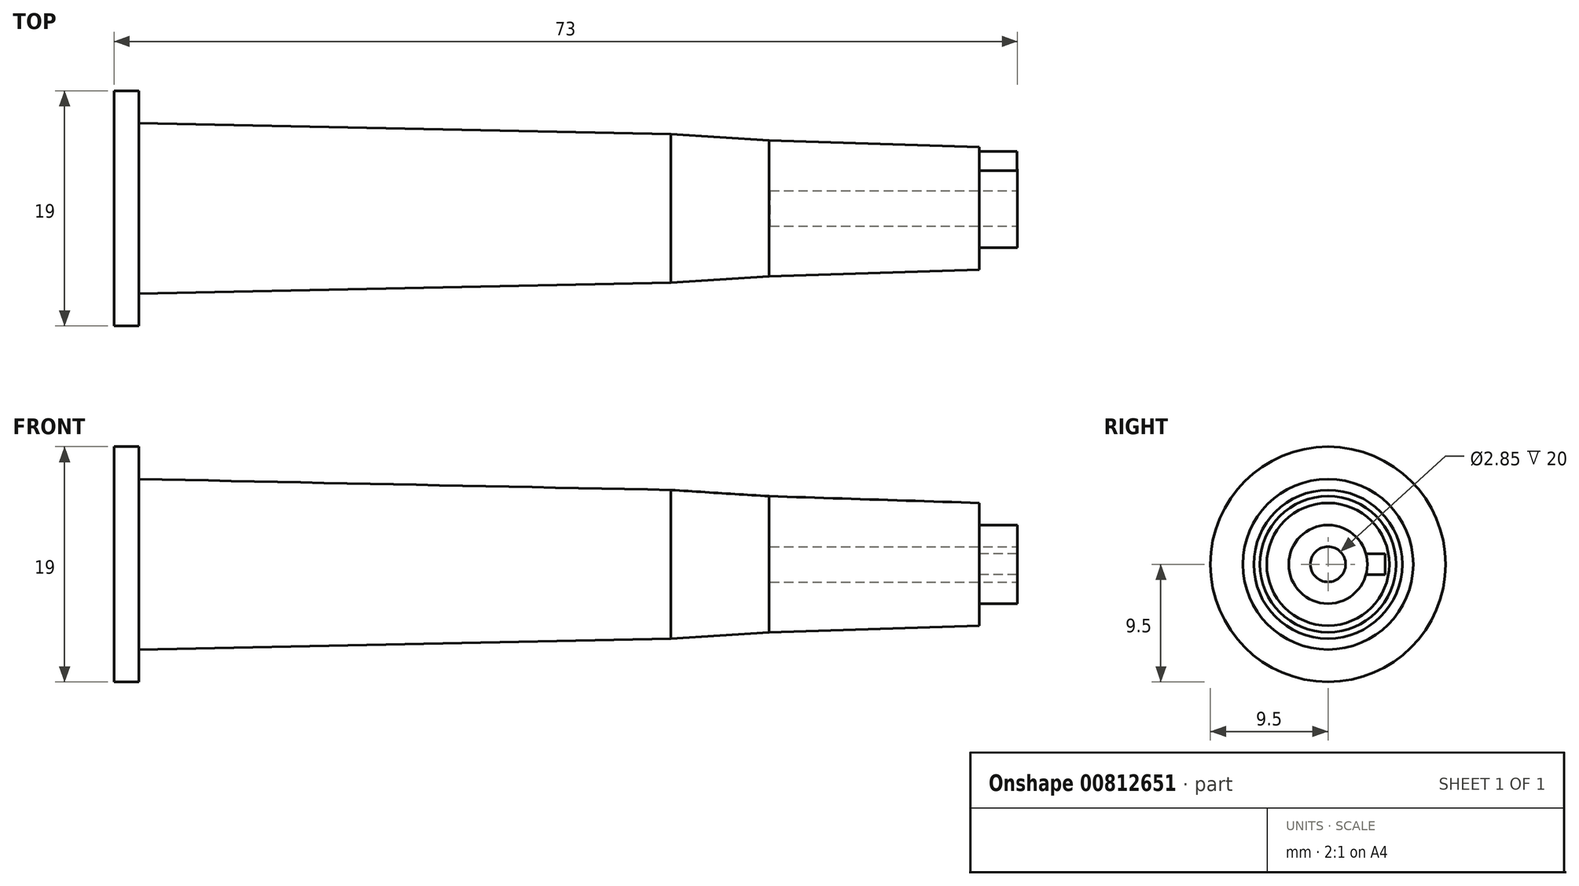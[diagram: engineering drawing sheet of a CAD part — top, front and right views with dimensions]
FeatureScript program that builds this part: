
annotation { "Feature Type Name" : "Feature", "Feature Type Description" : "" }
export const myFeature = defineFeature(function(context is Context, id is Id, definition is map)
    precondition{}
    {
        {
            var Q0;
            Q0=qCreatedBy(makeId("Front.planeOp"),FACE);
            var sketch = newSketch(context, id + "F0", { "sketchPlane" : qUnion([Q0])});
            skLineSegment(sketch, "E0", {"start": v(0, 0) * mm, "end": v(0, 9.5) * mm});
            skLineSegment(sketch, "E1", {"start": v(0, 0) * mm, "end": v(73, 0) * mm});
            skLineSegment(sketch, "E2.0", {"start": v(73, 0) * mm, "end": v(73, 3.18) * mm});
            skLineSegment(sketch, "E3.0", {"start": v(0, 9.5) * mm, "end": v(2, 9.5) * mm});
            skLineSegment(sketch, "E4", {"start": v(2, 6.88) * mm, "end": v(45, 6) * mm});
            skLineSegment(sketch, "E5.0", {"start": v(69.92, 3.18) * mm, "end": v(69.92, 4.96) * mm});
            skLineSegment(sketch, "E6", {"start": v(52.92, 5.5) * mm, "end": v(69.92, 4.96) * mm});
            skLineSegment(sketch, "E7.trimOffspring", {"start": v(69.92, 3.17) * mm, "end": v(73, 3.17) * mm});
            skLineSegment(sketch, "E8", {"start": v(45, 6) * mm, "end": v(52.92, 5.5) * mm});
            skLineSegment(sketch, "E9.trimOffspring", {"start": v(2, 6.88) * mm, "end": v(2, 9.5) * mm});
            skSolve(sketch);
        }
        {
            var Q0;
            Q0=makeQuery(id+"F0.imprint","IMPRINT",FACE,{"disambiguationData":[TD([[makeQuery(id+"F0.imprint","IMPRINT",EDGE,{"derivedFrom":sQuery(id+"F0.wireOp",EDGE,"E0")}),-1.0]])]});
            var Q1;
            Q1=sQuery(id+"F0.wireOp",EDGE,"E1");
            revolve(context, id + "F1", {"surfaceOperationType" : NewSurfaceOperationType.NEW, "entities" : qUnion([Q0]), "axis" : qUnion([Q1]), "revolveType" : RevolveType.FULL});
        }
        {
            var Q0;
            Q0=makeQuery(id+"F1.opRevolve","SWEPT_FACE",FACE,{"disambiguationData":[OSD([sQuery(id+"F0.wireOp",EDGE,"E5.0")])]});
            var sketch = newSketch(context, id + "F2", { "sketchPlane" : qUnion([Q0])});
            skLineSegment(sketch, "E10.0", {"start": v(4.61, 0.85) * mm, "end": v(4.61, -0.85) * mm});
            skLineSegment(sketch, "E11.0", {"start": v(3.06, -0.85) * mm, "end": v(4.61, -0.85) * mm});
            skLineSegment(sketch, "E12.0", {"start": v(3.06, 0.85) * mm, "end": v(4.61, 0.85) * mm});
            skPoint(sketch, "E13.orphan", {"position": v(0, 3.18) * mm});
            skPoint(sketch, "E14.start.orphan", {"position": v(0, 0) * mm});
            skCircle(sketch, "E15", {"center": v(0, 0) * mm, "radius": 3.18 * mm});
            skPoint(sketch, "E16.end.orphan", {"position": v(0, -3.18) * mm});
            skSolve(sketch);
        }
        {
            var Q0;
            Q0 = qSketchRegion(id + "F2", true);
            extrude(context, id + "F3", {"entities" : qUnion([Q0]), "operationType" : NewBodyOperationType.ADD, "depth" : 3.05 * mm, "offsetDistance" : 25 * mm});
        }
        {
            var Q0;
            Q0=makeQuery(id+"F1.opRevolve","SWEPT_FACE",FACE,{"disambiguationData":[OSD([sQuery(id+"F0.wireOp",EDGE,"E2.0")])]});
            var sketch = newSketch(context, id + "F4", { "sketchPlane" : qUnion([Q0])});
            skCircle(sketch, "E17", {"center": v(0, 0) * mm, "radius": 1.43 * mm});
            skSolve(sketch);
        }
        {
            var Q0;
            Q0=makeQuery(id+"F4.imprint","IMPRINT",FACE,{"disambiguationData":[TD([[makeQuery(id+"F4.imprint","IMPRINT",EDGE,{"derivedFrom":sQuery(id+"F4.wireOp",EDGE,"E17")}),1.0]])]});
            extrude(context, id + "F5", {"entities" : qUnion([Q0]), "operationType" : NewBodyOperationType.REMOVE, "oppositeDirection" : true, "depth" : 20 * mm, "offsetDistance" : 25 * mm});
        }
    });
